# Revit family: NBS_WallgateLtd_ShwrHds_SNC
name_source: partatom
category: Plumbing Fixtures
revit_build: Autodesk Revit 2014 (Build: 20130709_2115(x64)
units: mm (PartAtom-declared; Revit-internal decimal feet)

## types (1)
- SNC
    ActivationOptions = Push button, piezo touch button or infra red sensor
    AssetType = Fixed
    BIMObjectName = NBS_WallgateLtd_ShowerHeads_SNC
    Color = Stainless steel
    Description = Anti-ligature, anti vandal stainless steel ceiling mounted shower nozzle
    DrainSize = 0 mm  [stored 0 ft]
    DurationUnit = year
    Features = Hygienic and easily cleaned, highly vandal-resistant, anti-ligature
    Finish = Stainless Steel
    Form = Single function fixed head
    HasTray = No
    IfcExportAs = IfcSanitaryTerminalType
    IfcExportType = SHOWER
    IntegralAccessoryOptions = PBA Piezo Touch Buttons, PBA-IR Infra-Red Activation Sensors, WVPS Shower Water Valve Pack, CLS Key Lock Switches, WDC Electronic Controllers, SMVA Temperature Adjustable Showers, MV0001 Thermostatic Mixer Valve, MBS Manifold
    ManufacturerName = Wallgate Ltd
    ManufacturerURL = www.wallgate.com
    Material = Stainless steel
    MaterialThickness = 2 mm  [stored 0.00656168 ft]
    ModelNumber = SNC
    NBSCertification = www.nationalbimlibrary.com/cert/xzjsb4p1
    NBSDescription = Shower heads
    NBSReference = 45-35-70/333
    Name = ShowerHeads_SNC_WallgateLtd
    NominalDepth = 0 mm  [stored 0 ft]
    NominalHeight = 27 mm
    NominalLength = 130 mm  [stored 0.426509 ft]
    NominalWidth = 130 mm  [stored 0.426509 ft]
    ProductInformation = www.wallgate.com/products/showers-and-accessories/snc-ceiling-mount-shower-nozzles
    Shape = Circular
    ShowerHeadDescription = Flush stainless steel ceiling mount
    ShowerHeadMaterial = NBS_Concept
    ShowerType = Individual
    Size = 1.5 x 130 Ø x 26.5 mm
    Uniclass2 = 45-31-06/481
    Version = 1
    WarrantyDurationParts = 1
    WarrantyDurationUnit = year
    Weight = 0.5 kg

note: [stored X ft] marks values corroborated as IEEE doubles in the binary element streams (Revit-internal decimal feet)

## geometry (parser evidence)
native form markers: Sweep x1
no freeform markers — native parametric forms only
